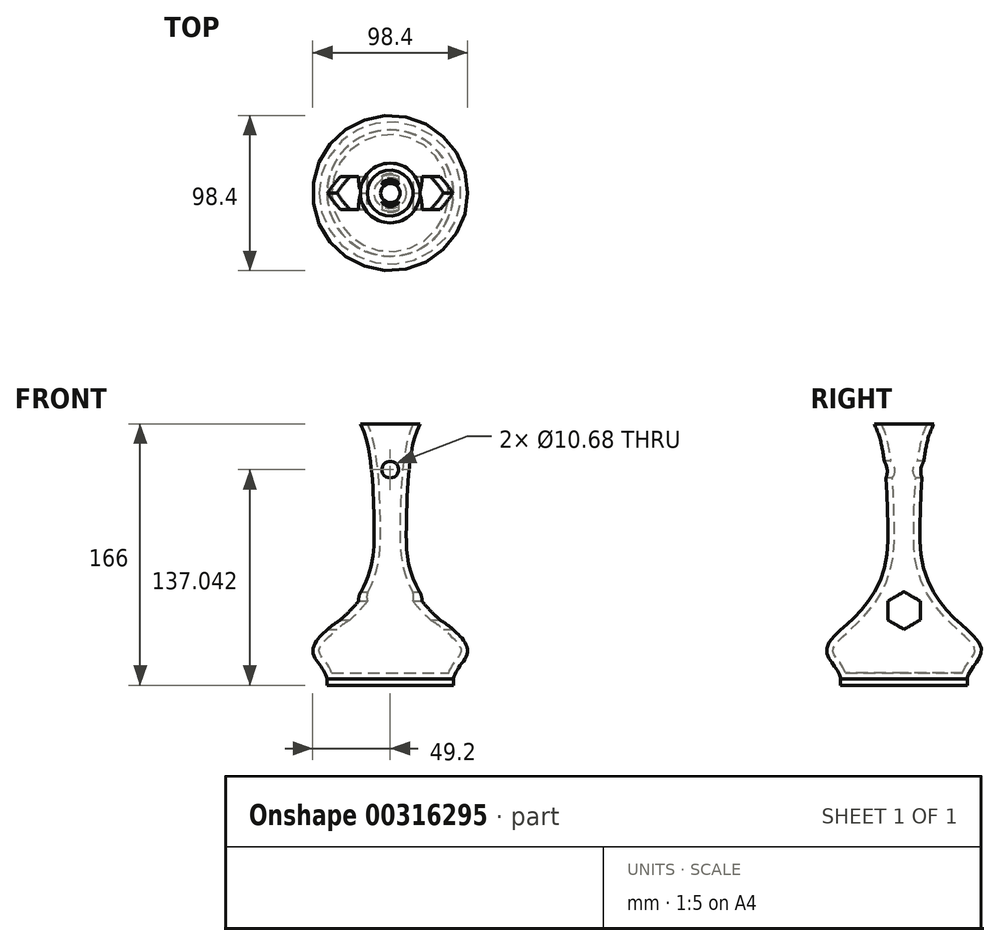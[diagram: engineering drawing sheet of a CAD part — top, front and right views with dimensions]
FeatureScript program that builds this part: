
annotation { "Feature Type Name" : "Feature", "Feature Type Description" : "" }
export const myFeature = defineFeature(function(context is Context, id is Id, definition is map)
    precondition{}
    {
        {
            var Q0;
            Q0=qCreatedBy(makeId("Top.planeOp"),FACE);
            var sketch = newSketch(context, id + "F0", { "sketchPlane" : qUnion([Q0])});
            skCircle(sketch, "E0", {"center": v(0, 0) * mm, "radius": 40 * mm});
            skSolve(sketch);
        }
        {
            var Q0;
            Q0=makeQuery(id+"F0.imprint","IMPRINT",FACE,{"disambiguationData":[TD([[makeQuery(id+"F0.imprint","IMPRINT",EDGE,{"derivedFrom":sQuery(id+"F0.wireOp",EDGE,"E0")}),1.0]])]});
            cPlane(context, id + "F1", {"entities" : qUnion([Q0]), "cplaneType" : CPlaneType.OFFSET, "offset" : 4 * mm, "width" : 150 * mm, "height" : 150 * mm});
        }
        {
            var Q0;
            Q0=qCreatedBy(id+"F1.planeOp",FACE);
            var sketch = newSketch(context, id + "F2", { "sketchPlane" : qUnion([Q0])});
            skCircle(sketch, "E1", {"center": v(0, 0) * mm, "radius": 41.51 * mm});
            skSolve(sketch);
        }
        {
            var Q0;
            Q0=makeQuery(id+"F2.imprint","IMPRINT",FACE,{"disambiguationData":[TD([[makeQuery(id+"F2.imprint","IMPRINT",EDGE,{"derivedFrom":sQuery(id+"F2.wireOp",EDGE,"E1")}),1.0]])]});
            cPlane(context, id + "F3", {"entities" : qUnion([Q0]), "cplaneType" : CPlaneType.OFFSET, "offset" : 6 * mm, "width" : 150 * mm, "height" : 150 * mm});
        }
        {
            var Q0;
            Q0=qCreatedBy(id+"F3.planeOp",FACE);
            var sketch = newSketch(context, id + "F4", { "sketchPlane" : qUnion([Q0])});
            skCircle(sketch, "E2", {"center": v(0, 0) * mm, "radius": 45.5 * mm});
            skSolve(sketch);
        }
        {
            var Q0;
            Q0=makeQuery(id+"F4.imprint","IMPRINT",FACE,{"disambiguationData":[TD([[makeQuery(id+"F4.imprint","IMPRINT",EDGE,{"derivedFrom":sQuery(id+"F4.wireOp",EDGE,"E2")}),1.0]])]});
            cPlane(context, id + "F5", {"entities" : qUnion([Q0]), "cplaneType" : CPlaneType.OFFSET, "offset" : 8 * mm, "width" : 150 * mm, "height" : 150 * mm});
        }
        {
            var Q0;
            Q0=qCreatedBy(id+"F5.planeOp",FACE);
            var sketch = newSketch(context, id + "F6", { "sketchPlane" : qUnion([Q0])});
            skCircle(sketch, "E3", {"center": v(0, 0) * mm, "radius": 49.2 * mm});
            skSolve(sketch);
        }
        {
            var Q0;
            Q0=makeQuery(id+"F6.imprint","IMPRINT",FACE,{"disambiguationData":[TD([[makeQuery(id+"F6.imprint","IMPRINT",EDGE,{"derivedFrom":sQuery(id+"F6.wireOp",EDGE,"E3")}),1.0]])]});
            cPlane(context, id + "F7", {"entities" : qUnion([Q0]), "cplaneType" : CPlaneType.OFFSET, "offset" : 6 * mm, "width" : 150 * mm, "height" : 150 * mm});
        }
        {
            var Q0;
            Q0=qCreatedBy(id+"F7.planeOp",FACE);
            var sketch = newSketch(context, id + "F8", { "sketchPlane" : qUnion([Q0])});
            skCircle(sketch, "E4", {"center": v(0, 0) * mm, "radius": 47 * mm});
            skSolve(sketch);
        }
        {
            var Q0;
            Q0=qCreatedBy(id+"F7.planeOp",FACE);
            cPlane(context, id + "F9", {"entities" : qUnion([Q0]), "cplaneType" : CPlaneType.OFFSET, "offset" : 6 * mm, "width" : 150 * mm, "height" : 150 * mm});
        }
        {
            var Q0;
            Q0=qCreatedBy(id+"F9.planeOp",FACE);
            var sketch = newSketch(context, id + "F10", { "sketchPlane" : qUnion([Q0])});
            skCircle(sketch, "E5", {"center": v(0, 0) * mm, "radius": 41.44 * mm});
            skSolve(sketch);
        }
        {
            var Q0;
            Q0=qCreatedBy(id+"F9.planeOp",FACE);
            cPlane(context, id + "F11", {"entities" : qUnion([Q0]), "cplaneType" : CPlaneType.OFFSET, "offset" : 16 * mm, "width" : 150 * mm, "height" : 150 * mm});
        }
        {
            var Q0;
            Q0=qCreatedBy(id+"F11.planeOp",FACE);
            var sketch = newSketch(context, id + "F12", { "sketchPlane" : qUnion([Q0])});
            skCircle(sketch, "E6", {"center": v(0, 0) * mm, "radius": 25.29 * mm});
            skSolve(sketch);
        }
        {
            var Q0;
            Q0=qCreatedBy(id+"F11.planeOp",FACE);
            cPlane(context, id + "F13", {"entities" : qUnion([Q0]), "cplaneType" : CPlaneType.OFFSET, "offset" : 25 * mm, "width" : 150 * mm, "height" : 150 * mm});
        }
        {
            var Q0;
            Q0=qCreatedBy(id+"F13.planeOp",FACE);
            var sketch = newSketch(context, id + "F14", { "sketchPlane" : qUnion([Q0])});
            skCircle(sketch, "E7", {"center": v(0, 0) * mm, "radius": 12.22 * mm});
            skSolve(sketch);
        }
        {
            var Q0;
            Q0=qCreatedBy(id+"F13.planeOp",FACE);
            cPlane(context, id + "F15", {"entities" : qUnion([Q0]), "cplaneType" : CPlaneType.OFFSET, "offset" : 25 * mm, "width" : 150 * mm, "height" : 150 * mm});
        }
        {
            var Q0;
            Q0=qCreatedBy(id+"F15.planeOp",FACE);
            var sketch = newSketch(context, id + "F16", { "sketchPlane" : qUnion([Q0])});
            skCircle(sketch, "E8", {"center": v(0, 0) * mm, "radius": 10.18 * mm});
            skSolve(sketch);
        }
        {
            var Q0;
            Q0=qCreatedBy(id+"F15.planeOp",FACE);
            cPlane(context, id + "F17", {"entities" : qUnion([Q0]), "cplaneType" : CPlaneType.OFFSET, "offset" : 25 * mm, "width" : 150 * mm, "height" : 150 * mm});
        }
        {
            var Q0;
            Q0=qCreatedBy(id+"F17.planeOp",FACE);
            var sketch = newSketch(context, id + "F18", { "sketchPlane" : qUnion([Q0])});
            skCircle(sketch, "E9", {"center": v(0, 0) * mm, "radius": 11 * mm});
            skSolve(sketch);
        }
        {
            var Q0;
            Q0=qCreatedBy(id+"F17.planeOp",FACE);
            cPlane(context, id + "F19", {"entities" : qUnion([Q0]), "cplaneType" : CPlaneType.OFFSET, "offset" : 25 * mm, "width" : 150 * mm, "height" : 150 * mm});
        }
        {
            var Q0;
            Q0=qCreatedBy(id+"F19.planeOp",FACE);
            var sketch = newSketch(context, id + "F20", { "sketchPlane" : qUnion([Q0])});
            skCircle(sketch, "E10", {"center": v(0, 0) * mm, "radius": 13.75 * mm});
            skSolve(sketch);
        }
        {
            var Q0;
            Q0=qCreatedBy(id+"F19.planeOp",FACE);
            cPlane(context, id + "F21", {"entities" : qUnion([Q0]), "cplaneType" : CPlaneType.OFFSET, "offset" : 10 * mm, "width" : 150 * mm, "height" : 150 * mm});
        }
        {
            var Q0;
            Q0=qCreatedBy(id+"F21.planeOp",FACE);
            var sketch = newSketch(context, id + "F22", { "sketchPlane" : qUnion([Q0])});
            skCircle(sketch, "E11", {"center": v(0, 0) * mm, "radius": 16.33 * mm});
            skSolve(sketch);
        }
        {
            var Q0;
            Q0=qCreatedBy(id+"F21.planeOp",FACE);
            cPlane(context, id + "F23", {"entities" : qUnion([Q0]), "cplaneType" : CPlaneType.OFFSET, "offset" : 6 * mm, "width" : 150 * mm, "height" : 150 * mm});
        }
        {
            var Q0;
            Q0=qCreatedBy(id+"F23.planeOp",FACE);
            var sketch = newSketch(context, id + "F24", { "sketchPlane" : qUnion([Q0])});
            skCircle(sketch, "E12", {"center": v(0, 0) * mm, "radius": 18.94 * mm});
            skSolve(sketch);
        }
        {
            var Q0;
            Q0=qSketchRegion(id+"F0",true);
            var Q1;
            Q1=qSketchRegion(id+"F2",true);
            var Q2;
            Q2=qSketchRegion(id+"F4",true);
            var Q3;
            Q3=qSketchRegion(id+"F6",true);
            var Q4;
            Q4=qSketchRegion(id+"F8",true);
            var Q5;
            Q5=qSketchRegion(id+"F10",true);
            var Q6;
            Q6=qSketchRegion(id+"F12",true);
            var Q7;
            Q7=qSketchRegion(id+"F14",true);
            var Q8;
            Q8=qSketchRegion(id+"F16",true);
            var Q9;
            Q9=qSketchRegion(id+"F18",true);
            var Q10;
            Q10=qSketchRegion(id+"F20",true);
            var Q11;
            Q11=qSketchRegion(id+"F22",true);
            var Q12;
            Q12=qSketchRegion(id+"F24",true);
            loft(context, id + "F25", {"sheetProfilesArray" : [{ "sheetProfileEntities" : qUnion([Q0]) }, { "sheetProfileEntities" : qUnion([Q1]) }, { "sheetProfileEntities" : qUnion([Q2]) }, { "sheetProfileEntities" : qUnion([Q3]) }, { "sheetProfileEntities" : qUnion([Q4]) }, { "sheetProfileEntities" : qUnion([Q5]) }, { "sheetProfileEntities" : qUnion([Q6]) }, { "sheetProfileEntities" : qUnion([Q7]) }, { "sheetProfileEntities" : qUnion([Q8]) }, { "sheetProfileEntities" : qUnion([Q9]) }, { "sheetProfileEntities" : qUnion([Q10]) }, { "sheetProfileEntities" : qUnion([Q11]) }, { "sheetProfileEntities" : qUnion([Q12]) }]});
        }
        {
            var Q0;
            Q0=makeQuery(id+"F25.opLoft","CAP_FACE",FACE,{"disambiguationData":[OSD([makeQuery(id+"F24.imprint","IMPRINT",FACE,{"disambiguationData":[TD([[makeQuery(id+"F24.imprint","IMPRINT",EDGE,{"derivedFrom":sQuery(id+"F24.wireOp",EDGE,"E12")}),1.0]])]})])],"isStart":true});
            shell(context, id + "F26", {"entities" : qUnion([Q0]), "thickness" : 4 * mm});
        }
        {
            var Q0;
            Q0=qCreatedBy(makeId("Top.planeOp"),FACE);
            var sketch = newSketch(context, id + "F27", { "sketchPlane" : qUnion([Q0])});
            skCircle(sketch, "E13", {"center": v(0, 0) * mm, "radius": 40.24 * mm});
            skSolve(sketch);
        }
        {
            var Q0;
            Q0=qSketchRegion(id+"F27",true);
            extrude(context, id + "F28", {"entities" : qUnion([Q0]), "operationType" : NewBodyOperationType.ADD, "oppositeDirection" : true, "depth" : 4 * mm});
        }
        {
            var Q0;
            Q0=qCreatedBy(makeId("Right.planeOp"),FACE);
            var sketch = newSketch(context, id + "F29", { "sketchPlane" : qUnion([Q0])});
            skCircle(sketch, "E14.cCircle", {"center": v(0, 43.5) * mm, "radius": 11.94 * mm, "construction": true});
            skLineSegment(sketch, "E14.0", {"start": v(0, 55.44) * mm, "end": v(10.34, 49.47) * mm});
            skLineSegment(sketch, "E14.1", {"start": v(10.34, 49.47) * mm, "end": v(10.34, 37.53) * mm});
            skLineSegment(sketch, "E14.2", {"start": v(10.34, 37.53) * mm, "end": v(0, 31.56) * mm});
            skLineSegment(sketch, "E14.3", {"start": v(0, 31.56) * mm, "end": v(-10.34, 37.53) * mm});
            skLineSegment(sketch, "E14.4", {"start": v(-10.34, 37.53) * mm, "end": v(-10.34, 49.47) * mm});
            skLineSegment(sketch, "E14.5", {"start": v(-10.34, 49.47) * mm, "end": v(0, 55.44) * mm});
            skPoint(sketch, "E15.center.orphan", {"position": v(0, 122.97) * mm});
            skSolve(sketch);
        }
        {
            var Q0;
            Q0 = qSketchRegion(id + "F29", true);
            var Q1;
            Q1 = qSketchRegion(id + "FBmWxguDaJttuCU_1", true);
            extrude(context, id + "F30", {"entities" : qUnion([Q0, Q1]), "operationType" : NewBodyOperationType.REMOVE, "endBound" : BoundingType.SYMMETRIC, "oppositeDirection" : true, "depth" : 88 * mm, "offsetDistance" : 25 * mm});
        }
        {
            var Q0;
            Q0=qCreatedBy(makeId("Front.planeOp"),FACE);
            var sketch = newSketch(context, id + "F31", { "sketchPlane" : qUnion([Q0])});
            skCircle(sketch, "E16", {"center": v(0, 133.04) * mm, "radius": 5.34 * mm});
            skSolve(sketch);
        }
        {
            var Q0;
            Q0 = qSketchRegion(id + "F31", true);
            extrude(context, id + "F32", {"entities" : qUnion([Q0]), "operationType" : NewBodyOperationType.REMOVE, "endBound" : BoundingType.SYMMETRIC, "oppositeDirection" : true, "depth" : 66 * mm, "offsetDistance" : 25 * mm});
        }
    });
